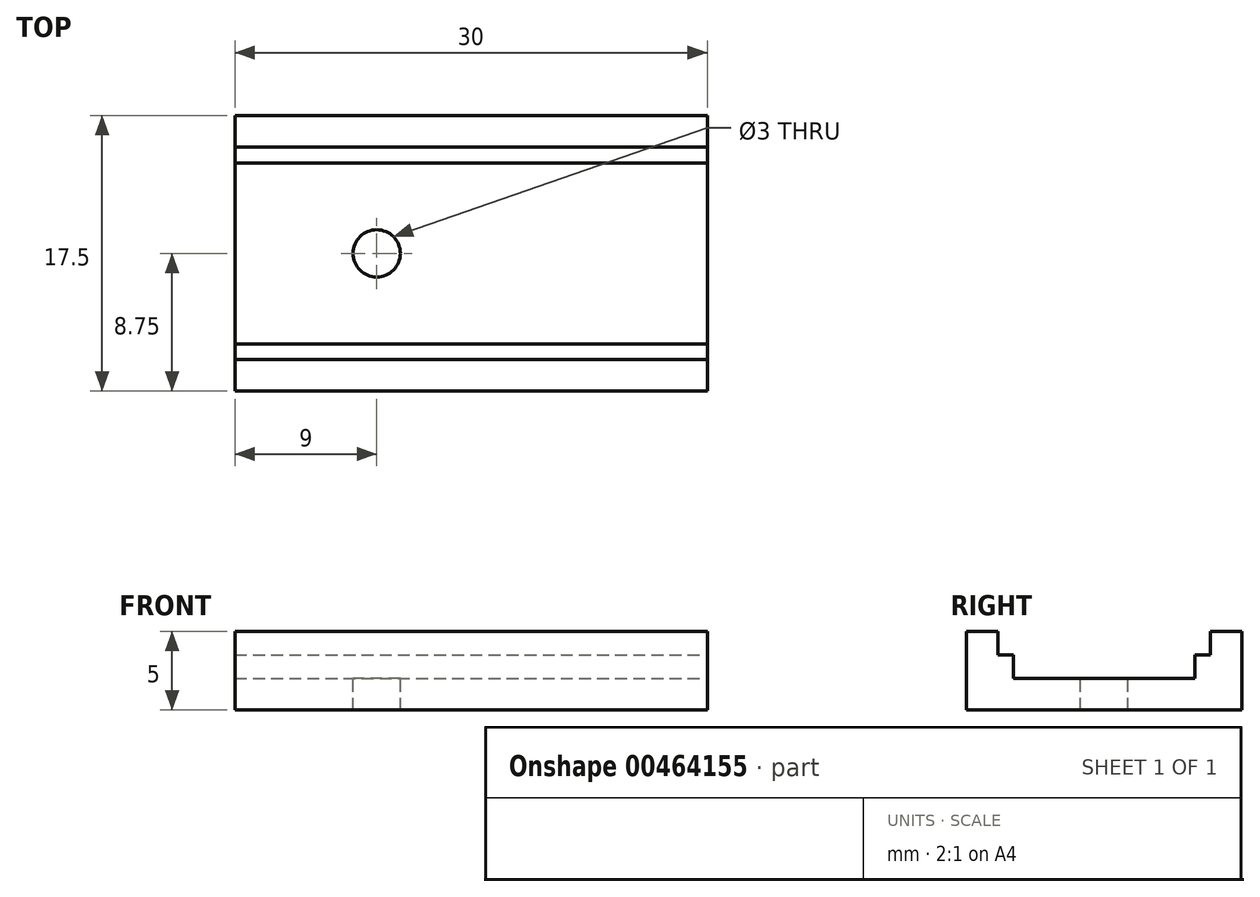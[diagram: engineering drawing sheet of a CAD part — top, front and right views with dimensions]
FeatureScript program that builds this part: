
annotation { "Feature Type Name" : "Feature", "Feature Type Description" : "" }
export const myFeature = defineFeature(function(context is Context, id is Id, definition is map)
    precondition{}
    {
        {
            var Q0;
            Q0=qCreatedBy(makeId("Top.planeOp"),FACE);
            var sketch = newSketch(context, id + "F0", { "sketchPlane" : qUnion([Q0])});
            skLineSegment(sketch, "E0.bottom", {"start": v(0, 0) * mm, "end": v(-30, 0) * mm});
            skLineSegment(sketch, "E0.top", {"start": v(0, 17.5) * mm, "end": v(-30, 17.5) * mm});
            skLineSegment(sketch, "E0.left", {"start": v(0, 0) * mm, "end": v(0, 17.5) * mm});
            skLineSegment(sketch, "E0.right", {"start": v(-30, 0) * mm, "end": v(-30, 17.5) * mm});
            skSolve(sketch);
        }
        {
            var Q0;
            Q0 = qSketchRegion(id + "F0", true);
            extrude(context, id + "F1", {"entities" : qUnion([Q0]), "depth" : 2 * mm, "offsetDistance" : 25 * mm});
        }
        {
            var Q0;
            Q0=makeQuery(id+"F1.opExtrude","CAP_FACE",FACE,{"disambiguationData":[OSD([sQuery(id+"F0.wireOp",EDGE,"E0.bottom"),sQuery(id+"F0.wireOp",EDGE,"E0.top"),sQuery(id+"F0.wireOp",EDGE,"E0.left"),sQuery(id+"F0.wireOp",EDGE,"E0.right")])],"isStart":false});
            var sketch = newSketch(context, id + "F2", { "sketchPlane" : qUnion([Q0])});
            skCircle(sketch, "E1", {"center": v(-21, 8.75) * mm, "radius": 1.5 * mm});
            skSolve(sketch);
        }
        {
            var Q0;
            Q0 = qSketchRegion(id + "F2", true);
            extrude(context, id + "F3", {"entities" : qUnion([Q0]), "operationType" : NewBodyOperationType.REMOVE, "oppositeDirection" : true, "depth" : 25 * mm, "offsetDistance" : 25 * mm});
        }
        {
            var Q0;
            Q0=makeQuery(id+"F1.opExtrude","CAP_FACE",FACE,{"disambiguationData":[OSD([sQuery(id+"F0.wireOp",EDGE,"E0.bottom"),sQuery(id+"F0.wireOp",EDGE,"E0.top"),sQuery(id+"F0.wireOp",EDGE,"E0.left"),sQuery(id+"F0.wireOp",EDGE,"E0.right")])],"isStart":false});
            var sketch = newSketch(context, id + "F4", { "sketchPlane" : qUnion([Q0])});
            skLineSegment(sketch, "E2.bottom", {"start": v(-30, 17.5) * mm, "end": v(0, 17.5) * mm});
            skLineSegment(sketch, "E2.top", {"start": v(-30, 15.5) * mm, "end": v(0, 15.5) * mm});
            skLineSegment(sketch, "E2.left", {"start": v(-30, 17.5) * mm, "end": v(-30, 15.5) * mm});
            skLineSegment(sketch, "E2.right", {"start": v(0, 17.5) * mm, "end": v(0, 15.5) * mm});
            skLineSegment(sketch, "E3.bottom", {"start": v(-30, 0) * mm, "end": v(0, 0) * mm});
            skLineSegment(sketch, "E3.top", {"start": v(-30, 2) * mm, "end": v(0, 2) * mm});
            skLineSegment(sketch, "E3.left", {"start": v(-30, 0) * mm, "end": v(-30, 2) * mm});
            skLineSegment(sketch, "E3.right", {"start": v(0, 0) * mm, "end": v(0, 2) * mm});
            skSolve(sketch);
        }
        {
            var Q0;
            Q0 = qSketchRegion(id + "F4", true);
            extrude(context, id + "F5", {"entities" : qUnion([Q0]), "operationType" : NewBodyOperationType.ADD, "depth" : 3 * mm, "offsetDistance" : 25 * mm});
        }
        {
            var Q0;
            Q0=makeQuery(id+"F1.opExtrude","CAP_FACE",FACE,{"disambiguationData":[OSD([sQuery(id+"F0.wireOp",EDGE,"E0.bottom"),sQuery(id+"F0.wireOp",EDGE,"E0.top"),sQuery(id+"F0.wireOp",EDGE,"E0.left"),sQuery(id+"F0.wireOp",EDGE,"E0.right")])],"isStart":false});
            var sketch = newSketch(context, id + "F6", { "sketchPlane" : qUnion([Q0])});
            skLineSegment(sketch, "E4.bottom", {"start": v(-30, 15.5) * mm, "end": v(0, 15.5) * mm});
            skLineSegment(sketch, "E4.top", {"start": v(-30, 14.5) * mm, "end": v(0, 14.5) * mm});
            skLineSegment(sketch, "E4.left", {"start": v(-30, 15.5) * mm, "end": v(-30, 14.5) * mm});
            skLineSegment(sketch, "E4.right", {"start": v(0, 15.5) * mm, "end": v(0, 14.5) * mm});
            skLineSegment(sketch, "E5.bottom", {"start": v(-30, 2) * mm, "end": v(0, 2) * mm});
            skLineSegment(sketch, "E5.top", {"start": v(-30, 3) * mm, "end": v(0, 3) * mm});
            skLineSegment(sketch, "E5.left", {"start": v(-30, 2) * mm, "end": v(-30, 3) * mm});
            skLineSegment(sketch, "E5.right", {"start": v(0, 2) * mm, "end": v(0, 3) * mm});
            skSolve(sketch);
        }
        {
            var Q0;
            Q0 = qSketchRegion(id + "F6", true);
            extrude(context, id + "F7", {"entities" : qUnion([Q0]), "operationType" : NewBodyOperationType.ADD, "depth" : 1.5 * mm, "offsetDistance" : 25 * mm});
        }
    });
